# Revit family: Faucet_Touchless-Lavatory-KOHLER-Geometric-K-13467_1
name_source: partatom
category: Plumbing Fixtures
units: mm (PartAtom-declared; Revit-internal decimal feet)

## family parameters
Cut with Voids When Loaded = No
Host = Face
OmniClass Number = 23.31.11.00
OmniClass Title = Faucets
Part Type = Normal
Room Calculation Point = No
Round Connector Dimension = Use Diameter
Shared = No

## types (2) — shared parameters
Assembly Code = D2010
CW Connection = Yes
Cold Water Inlet = Cold Water Inlet
Date Modified = 04/17/2023
Default Elevation = 36"
Drain Included = No
Faucet Hole Spacing = 0"
Finish = Kohler-Metal-CP-Polished_Chrome
HW Connection = Yes
Handle Clearance = 0"
Height = 5 5/16"
Hot Water Inlet = Hot Water Inlet
Length = 5 5/16"
Manufacturer = Kohler Co.
Master Format 2014 = 22 41 39
Master Format 2014 Name = Residential Faucets, Supplies, and Trim
Material = Premium Metal Construction
Pressure = 60.00 psi
Product Documentation Link = https://www.us.kohler.com
Product Name = Geometric
Product Page URL = http://www.us.kohler.com
Spout Reach = 5 5/16"
URL = https://www.us.kohler.com
Vent Connection = No
Waste Connection = No
Waste Water Outlet = Waste Water Outlet
WaterSense Certified = No
Width = 2 7/16"

## per-type parameters (varying)
| type | ADA Compliant | Description | Flow Rate | Model | Type |
| 0.5GPM, CP-Polished Chrome | Yes | Touchless single-hole lavatory sink faucet with Insight sensor technology, DC-powered, 0.5 gpm | 1 GPM | K-13467-CP | 2 |
| 0.35GPM, CP-Polished Chrome | No | INSIGHT DC 0.35GPM | 0 GPM | K-13467-SATA-CP | 1 |

## geometry (parser evidence)
native form markers: Sweep x5
no freeform markers — native parametric forms only
